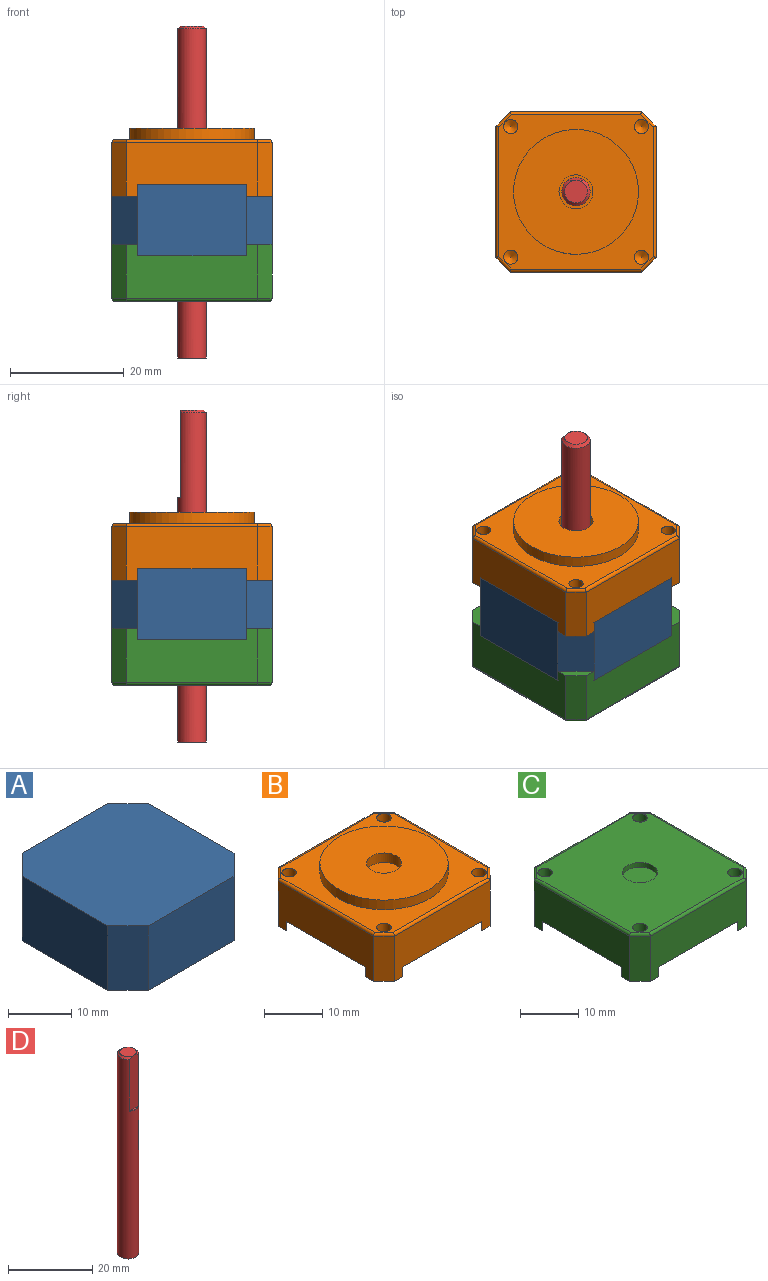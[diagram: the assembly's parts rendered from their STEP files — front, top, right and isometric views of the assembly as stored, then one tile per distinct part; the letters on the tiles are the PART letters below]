
ASSEMBLY  parts=4 mates=3
PART A: 10 faces, bbox 28.2x28.2x12.5 mm
  f0: plane 19.2x12.5mm, normal (0,1,0), area 240mm2, adj f1,f7,f8,f9
  f1: plane 12.5x4.5mm, normal (-0.71,0.71,0), area 79.5mm2, adj f0,f2,f8,f9
  f2: plane 19.2x12.5mm, normal (-1,0,0), area 240mm2, adj f1,f3,f8,f9
  f3: plane 12.5x4.5mm, normal (-0.71,-0.71,0), area 79.5mm2, adj f2,f4,f8,f9
  f4: plane 19.2x12.5mm, normal (0,-1,0), area 240mm2, adj f3,f5,f8,f9
  f5: plane 12.5x4.5mm, normal (0.71,-0.71,0), area 79.5mm2, adj f4,f6,f8,f9
  f6: plane 19.2x12.5mm, normal (1,0,0), area 240mm2, adj f5,f7,f8,f9
  f7: plane 12.5x4.5mm, normal (0.71,0.71,0), area 79.5mm2, adj f0,f6,f8,f9
  f8: plane 28.2x28.2mm, normal (0,0,1), area 754.7mm2, adj f0,f1,f2,f3,f4,f5,f6,f7
  f9: plane 28.2x28.2mm, normal (0,0,-1), area 754.7mm2, adj f0,f1,f2,f3,f4,f5,f6,f7
PART B: 38 faces, bbox 28.2x28.2x12 mm
  f0: plane 28.2x28.2mm, normal (0,0,-1), area 754.7mm2, adj f1,f3,f5,f7,f14,f16,f18,f20
  f1: plane 23.2x9.5mm, normal (0,-1,0), area 182mm2, adj f0,f2,f8,f16,f17,f20,f21,f37
  f2: plane 9.5x2.5mm, normal (0.71,-0.71,0), area 33.6mm2, adj f1,f3,f17,f35
  f3: plane 23.2x9.5mm, normal (1,0,0), area 182mm2, adj f0,f2,f4,f14,f15,f16,f17,f33
  f4: plane 9.5x2.5mm, normal (0.71,0.71,0), area 33.6mm2, adj f3,f5,f15,f31
  f5: plane 23.2x9.5mm, normal (0,1,0), area 182mm2, adj f0,f4,f6,f14,f15,f18,f19,f30
  f6: plane 9.5x2.5mm, normal (-0.71,0.71,0), area 33.6mm2, adj f5,f7,f19,f32
  f7: plane 23.2x9.5mm, normal (-1,0,0), area 182mm2, adj f0,f6,f8,f18,f19,f20,f21,f34
  f8: plane 9.5x2.5mm, normal (-0.71,-0.71,0), area 33.6mm2, adj f1,f7,f21,f36
  f9: plane 27.2x27.2mm, normal (0,0,1), area 330.3mm2, adj f11,f23,f25,f27,f29,f30,f31,f32
  f10: cylinder r=3mm len=6mm, axis (0,0,-1), area 37.7mm2, adj f12,f13
  f11: cylinder r=11mm len=22mm, axis (0,0,-1), area 138.2mm2, adj f9,f12
  f12: plane 22x22mm, normal (0,0,1), area 351.9mm2, adj f10,f11
  f13: plane 6x6mm, normal (0,0,1), area 28.3mm2, adj f10
  f14: plane 4.5x4.5mm, normal (-0.71,-0.71,0), area 12.7mm2, adj f0,f3,f5,f15
  f15: plane 4.5x4.5mm, normal (0,0,-1), area 7mm2, adj f3,f4,f5,f14
  f16: plane 4.5x4.5mm, normal (-0.71,0.71,0), area 12.7mm2, adj f0,f1,f3,f17
  f17: plane 4.5x4.5mm, normal (0,0,-1), area 7mm2, adj f1,f2,f3,f16
  f18: plane 4.5x4.5mm, normal (0.71,-0.71,0), area 12.7mm2, adj f0,f5,f7,f19
  f19: plane 4.5x4.5mm, normal (0,0,-1), area 7mm2, adj f5,f6,f7,f18
  f20: plane 4.5x4.5mm, normal (0.71,0.71,0), area 12.7mm2, adj f0,f1,f7,f21
  f21: plane 4.5x4.5mm, normal (0,0,-1), area 7mm2, adj f1,f7,f8,f20
  f22: cone r=0mm half-angle=59deg, axis (0,0,1), area 5.7mm2, adj f23
  f23: cylinder r=1.25mm len=3mm, axis (0,0,1), area 23.6mm2, adj f9,f22
  f24: cone r=0mm half-angle=59deg, axis (0,0,1), area 5.7mm2, adj f25
  f25: cylinder r=1.25mm len=3mm, axis (0,0,1), area 23.6mm2, adj f9,f24
  f26: cone r=0mm half-angle=59deg, axis (0,0,1), area 5.7mm2, adj f27
  f27: cylinder r=1.25mm len=3mm, axis (0,0,1), area 23.6mm2, adj f9,f26
  f28: cone r=0mm half-angle=59deg, axis (0,0,1), area 5.7mm2, adj f29
  f29: cylinder r=1.25mm len=3mm, axis (0,0,1), area 23.6mm2, adj f9,f28
  f30: cylinder r=0.5mm len=23.2mm, axis (-1,0,0), area 18.1mm2, adj f5,f9,f31,f32
  f31: cylinder r=0.5mm len=2.85mm, axis (-0.71,0.71,0), area 2.7mm2, adj f4,f9,f30,f33
  f32: cylinder r=0.5mm len=2.85mm, axis (-0.71,-0.71,0), area 2.7mm2, adj f6,f9,f30,f34
  f33: cylinder r=0.5mm len=23.2mm, axis (0,1,0), area 18.1mm2, adj f3,f9,f31,f35
  f34: cylinder r=0.5mm len=23.2mm, axis (0,-1,0), area 18.1mm2, adj f7,f9,f32,f36
  f35: cylinder r=0.5mm len=2.85mm, axis (0.71,0.71,0), area 2.7mm2, adj f2,f9,f33,f37
  f36: cylinder r=0.5mm len=2.85mm, axis (0.71,-0.71,0), area 2.7mm2, adj f8,f9,f34,f37
  f37: cylinder r=0.5mm len=23.2mm, axis (1,0,0), area 18.1mm2, adj f1,f9,f35,f36
PART C: 36 faces, bbox 28.2x28.2x10 mm
  f0: plane 28.2x28.2mm, normal (0,0,-1), area 754.7mm2, adj f1,f3,f5,f7,f12,f14,f16,f18
  f1: plane 23.2x9.5mm, normal (0,1,0), area 182mm2, adj f0,f2,f8,f14,f15,f18,f19,f30
  f2: plane 9.5x2.5mm, normal (-0.71,0.71,0), area 33.6mm2, adj f1,f3,f19,f32
  f3: plane 23.2x9.5mm, normal (-1,0,0), area 182mm2, adj f0,f2,f4,f16,f17,f18,f19,f34
  f4: plane 9.5x2.5mm, normal (-0.71,-0.71,0), area 33.6mm2, adj f3,f5,f17,f35
  f5: plane 23.2x9.5mm, normal (0,-1,0), area 182mm2, adj f0,f4,f6,f12,f13,f16,f17,f33
  f6: plane 9.5x2.5mm, normal (0.71,-0.71,0), area 33.6mm2, adj f5,f7,f13,f31
  f7: plane 23.2x9.5mm, normal (1,0,0), area 182mm2, adj f0,f6,f8,f12,f13,f14,f15,f29
  f8: plane 9.5x2.5mm, normal (0.71,0.71,0), area 33.6mm2, adj f1,f7,f15,f28
  f9: plane 27.2x27.2mm, normal (0,0,1), area 682.2mm2, adj f10,f21,f23,f25,f27,f28,f29,f30
  f10: cylinder r=3mm len=6mm, axis (0,0,1), area 18.8mm2, adj f9,f11
  f11: plane 6x6mm, normal (0,0,1), area 28.3mm2, adj f10
  f12: plane 4.5x4.5mm, normal (-0.71,0.71,0), area 12.7mm2, adj f0,f5,f7,f13
  f13: plane 4.5x4.5mm, normal (0,0,-1), area 7mm2, adj f5,f6,f7,f12
  f14: plane 4.5x4.5mm, normal (-0.71,-0.71,0), area 12.7mm2, adj f0,f1,f7,f15
  f15: plane 4.5x4.5mm, normal (0,0,-1), area 7mm2, adj f1,f7,f8,f14
  f16: plane 4.5x4.5mm, normal (0.71,0.71,0), area 12.7mm2, adj f0,f3,f5,f17
  f17: plane 4.5x4.5mm, normal (0,0,-1), area 7mm2, adj f3,f4,f5,f16
  f18: plane 4.5x4.5mm, normal (0.71,-0.71,0), area 12.7mm2, adj f0,f1,f3,f19
  f19: plane 4.5x4.5mm, normal (0,0,-1), area 7mm2, adj f1,f2,f3,f18
  f20: cone r=0mm half-angle=59deg, axis (0,0,1), area 5.7mm2, adj f21
  f21: cylinder r=1.25mm len=3mm, axis (0,0,1), area 23.6mm2, adj f9,f20
  f22: cone r=0mm half-angle=59deg, axis (0,0,1), area 5.7mm2, adj f23
  f23: cylinder r=1.25mm len=3mm, axis (0,0,1), area 23.6mm2, adj f9,f22
  f24: cone r=0mm half-angle=59deg, axis (0,0,1), area 5.7mm2, adj f25
  f25: cylinder r=1.25mm len=3mm, axis (0,0,1), area 23.6mm2, adj f9,f24
  f26: cone r=0mm half-angle=59deg, axis (0,0,1), area 5.7mm2, adj f27
  f27: cylinder r=1.25mm len=3mm, axis (0,0,1), area 23.6mm2, adj f9,f26
  f28: cylinder r=0.5mm len=2.85mm, axis (-0.71,0.71,0), area 2.7mm2, adj f8,f9,f29,f30
  f29: cylinder r=0.5mm len=23.2mm, axis (0,1,0), area 18.1mm2, adj f7,f9,f28,f31
  f30: cylinder r=0.5mm len=23.2mm, axis (-1,0,0), area 18.1mm2, adj f1,f9,f28,f32
  f31: cylinder r=0.5mm len=2.85mm, axis (0.71,0.71,0), area 2.7mm2, adj f6,f9,f29,f33
  f32: cylinder r=0.5mm len=2.85mm, axis (-0.71,-0.71,0), area 2.7mm2, adj f2,f9,f30,f34
  f33: cylinder r=0.5mm len=23.2mm, axis (1,0,0), area 18.1mm2, adj f5,f9,f31,f35
  f34: cylinder r=0.5mm len=23.2mm, axis (0,-1,0), area 18.1mm2, adj f3,f9,f32,f35
  f35: cylinder r=0.5mm len=2.85mm, axis (0.71,-0.71,0), area 2.7mm2, adj f4,f9,f33,f34
PART D: 6 faces, bbox 5x5x58.5 mm
  f0: cylinder r=2.5mm len=58mm, axis (0,0,-1), area 862.8mm2, adj f2,f3,f4,f5
  f1: plane 4x4mm, normal (0,0,1), area 12.6mm2, adj f4
  f2: plane 15.5x3mm, normal (0,-1,0), area 46mm2, adj f0,f3,f4
  f3: plane 3x0.5mm, normal (0,0,1), area 1mm2, adj f0,f2
  f4: cone r=2mm half-angle=45deg, axis (0,0,-1), area 8.6mm2, adj f0,f1,f2
  f5: plane 5x5mm, normal (0,0,-1), area 19.6mm2, adj f0
PLACE A rot(axis=(0,0,1),180deg) t=(25.9,0,-6.25)mm
PLACE B rot(axis=(0,0,-1),180deg) t=(-14.1,0,14.25)mm
PLACE C rot(axis=(0,1,0),180deg) t=(-64.1,0,-14.25)mm
PLACE D rot(axis=(0,0,-1),179.7deg) t=(-13.95,-30,14.25)mm
MATE fastened B.f10 <-> A.f8  axis (0,0,-1) through (-14.1,0,6.25)mm
MATE fastened A.f9 <-> C.f10  axis (0,0,-1) through (-14.1,0,-6.25)mm
MATE revolute D.f0 <-> B.f10  axis (0,0,-1) through (-14.1,0,14.25)mm
